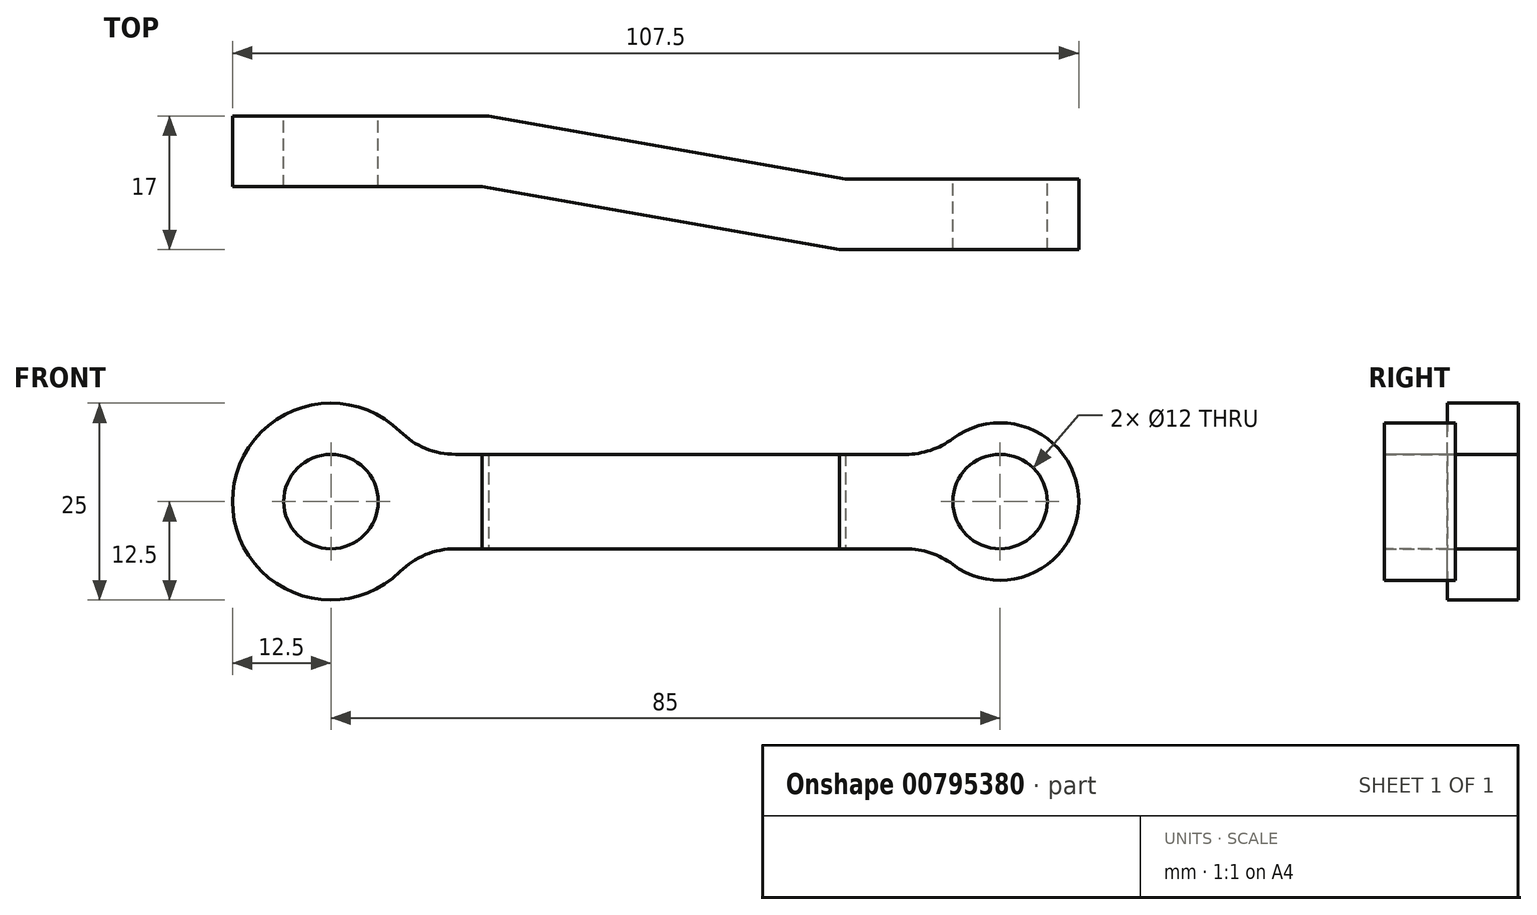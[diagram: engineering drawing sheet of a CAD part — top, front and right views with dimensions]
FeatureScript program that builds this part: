
annotation { "Feature Type Name" : "Feature", "Feature Type Description" : "" }
export const myFeature = defineFeature(function(context is Context, id is Id, definition is map)
    precondition{}
    {
        {
            var Q0;
            Q0=qCreatedBy(makeId("Front.planeOp"),FACE);
            var sketch = newSketch(context, id + "F0", { "sketchPlane" : qUnion([Q0])});
            skArc(sketch, "E0", {"start": v(10.97, 6) * mm, "mid": v(-12.5, 0) * mm, "end": v(10.97, -6) * mm});
            skArc(sketch, "E1", {"start": v(77, -6) * mm, "mid": v(95, 0) * mm, "end": v(77, 6) * mm});
            skLineSegment(sketch, "E2", {"start": v(0, 0) * mm, "end": v(85, 0) * mm, "construction": true});
            skLineSegment(sketch, "E3", {"start": v(77, 6) * mm, "end": v(10.97, 6) * mm});
            skLineSegment(sketch, "E4.MirrorCS", {"start": v(77, -6) * mm, "end": v(10.97, -6) * mm});
            skCircle(sketch, "E5", {"center": v(0, 0) * mm, "radius": 6 * mm});
            skCircle(sketch, "E6", {"center": v(85, 0) * mm, "radius": 6 * mm});
            skSolve(sketch);
        }
        {
            var Q0;
            Q0=makeQuery(id+"F0.imprint","IMPRINT",FACE,{"disambiguationData":[TD([[makeQuery(id+"F0.imprint","IMPRINT",EDGE,{"derivedFrom":sQuery(id+"F0.wireOp",EDGE,"E0")}),1.0]])]});
            extrude(context, id + "F1", {"entities" : qUnion([Q0]), "depth" : 25 * mm, "offsetDistance" : 25 * mm});
        }
        {
            var Q0;
            Q0=qCreatedBy(makeId("Top.planeOp"),FACE);
            var sketch = newSketch(context, id + "F2", { "sketchPlane" : qUnion([Q0])});
            skLineSegment(sketch, "E7", {"start": v(-12.5, 0) * mm, "end": v(20, 0) * mm});
            skLineSegment(sketch, "E8", {"start": v(20, 0) * mm, "end": v(65.37, -8) * mm});
            skLineSegment(sketch, "E9", {"start": v(65.37, -8) * mm, "end": v(95, -8) * mm});
            skLineSegment(sketch, "E10.0", {"start": v(64.58, -17) * mm, "end": v(95, -17) * mm});
            skLineSegment(sketch, "E10.1", {"start": v(19.21, -9) * mm, "end": v(64.58, -17) * mm});
            skLineSegment(sketch, "E10.2", {"start": v(-12.5, -9) * mm, "end": v(19.21, -9) * mm});
            skLineSegment(sketch, "E11", {"start": v(-12.5, -9) * mm, "end": v(-12.5, 0) * mm});
            skLineSegment(sketch, "E12", {"start": v(95, -17) * mm, "end": v(95, -8) * mm});
            skLineSegment(sketch, "E13", {"start": v(-12.5, -25) * mm, "end": v(-12.5, 0) * mm});
            skLineSegment(sketch, "E14.0.0", {"start": v(77, 0) * mm, "end": v(95, 0) * mm});
            skLineSegment(sketch, "E14.0.1", {"start": v(77, 0) * mm, "end": v(77, -25) * mm});
            skSolve(sketch);
        }
        {
            var Q0;
            Q0 = qSketchRegion(id + "F2", true);
            extrude(context, id + "F3", {"entities" : qUnion([Q0]), "operationType" : NewBodyOperationType.INTERSECT, "endBound" : BoundingType.SYMMETRIC, "depth" : 25 * mm, "offsetDistance" : 25 * mm});
        }
        {
            var Q0;
            Q0=makeQuery(id+"F1.opExtrude","SWEPT_EDGE",EDGE,{"disambiguationData":[OSD([sQuery(id+"F0.wireOp",EDGE,"E0"),sQuery(id+"F0.wireOp",EDGE,"E3")])]});
            var Q1;
            Q1=makeQuery(id+"F1.opExtrude","SWEPT_EDGE",EDGE,{"disambiguationData":[OSD([sQuery(id+"F0.wireOp",EDGE,"E1"),sQuery(id+"F0.wireOp",EDGE,"E3")])]});
            var Q2;
            Q2=makeQuery(id+"F3.boolean.opBoolean","COPY",EDGE,{"derivedFrom":makeQuery(id+"F3.boolean.toolComplement.opBoolean","COPY",EDGE,{"derivedFrom":makeQuery(id+"F3.opExtrude","SWEPT_EDGE",EDGE,{"disambiguationData":[OSD([sQuery(id+"F2.wireOp",EDGE,"E7"),sQuery(id+"F2.wireOp",EDGE,"E8")])]})})});
            var Q3;
            Q3=makeQuery(id+"F3.boolean.opBoolean","COPY",EDGE,{"derivedFrom":makeQuery(id+"F3.boolean.toolComplement.opBoolean","COPY",EDGE,{"derivedFrom":makeQuery(id+"F3.opExtrude","SWEPT_EDGE",EDGE,{"disambiguationData":[OSD([sQuery(id+"F2.wireOp",EDGE,"E8"),sQuery(id+"F2.wireOp",EDGE,"E9")])]})})});
            var Q4;
            Q4=makeQuery(id+"F1.opExtrude","SWEPT_EDGE",EDGE,{"disambiguationData":[OSD([sQuery(id+"F0.wireOp",EDGE,"E1"),sQuery(id+"F0.wireOp",EDGE,"E4.MirrorCS")])]});
            var Q5;
            Q5=makeQuery(id+"F1.opExtrude","SWEPT_EDGE",EDGE,{"disambiguationData":[OSD([sQuery(id+"F0.wireOp",EDGE,"E0"),sQuery(id+"F0.wireOp",EDGE,"E4.MirrorCS")])]});
            var Q6;
            Q6=makeQuery(id+"F3.boolean.opBoolean","COPY",EDGE,{"derivedFrom":makeQuery(id+"F3.boolean.toolComplement.opBoolean","COPY",EDGE,{"derivedFrom":makeQuery(id+"F3.opExtrude","SWEPT_EDGE",EDGE,{"disambiguationData":[OSD([sQuery(id+"F2.wireOp",EDGE,"E10.0"),sQuery(id+"F2.wireOp",EDGE,"E10.1")])]})})});
            var Q7;
            Q7=makeQuery(id+"F3.boolean.opBoolean","COPY",EDGE,{"derivedFrom":makeQuery(id+"F3.boolean.toolComplement.opBoolean","COPY",EDGE,{"derivedFrom":makeQuery(id+"F3.opExtrude","SWEPT_EDGE",EDGE,{"disambiguationData":[OSD([sQuery(id+"F2.wireOp",EDGE,"E10.1"),sQuery(id+"F2.wireOp",EDGE,"E10.2")])]})})});
            fillet(context, id + "F4", {"entities" : qUnion([Q0, Q1, Q2, Q3, Q4, Q5, Q6, Q7]), "radius" : 10 * mm, "tangentPropagation" : true, "allowEdgeOverflow" : false});
        }
    });
